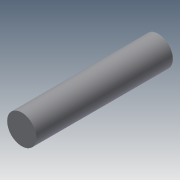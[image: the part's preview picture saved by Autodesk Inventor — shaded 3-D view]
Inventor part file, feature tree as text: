
AUTODESK INVENTOR PART (.ipt)
format: ipt  version: 2013 (Build 170138000, 138)  size: 68,096 bytes
history: native  units: mm
features: extrude x1, sketch x1
ambient origin geometry x8: Origin, YZ Plane, XZ Plane, XY Plane, X Axis, Y Axis, Z Axis, Center Point
bodies: Solid1 (feature_tree)
feature tree (2):
  extrude  "Extrusion1"  Depth=28.0mm TaperAngle=0.0deg
  sketch  "Sketch1"  dims[d0=6.0mm d1=28.0mm d2=0.0mm]
